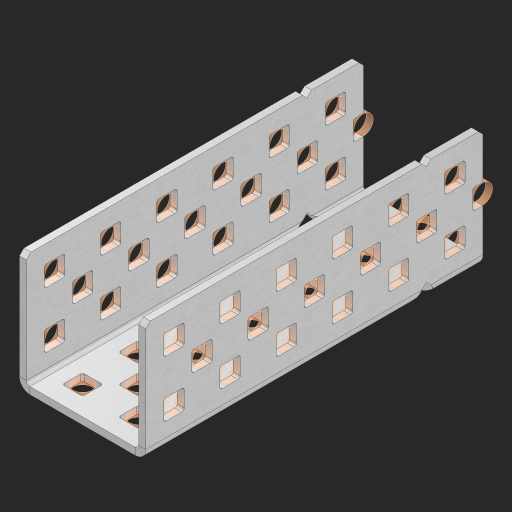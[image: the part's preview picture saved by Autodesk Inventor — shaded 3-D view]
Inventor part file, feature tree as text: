
AUTODESK INVENTOR PART (.ipt)
format: ipt  version: 2023 (Build 270158000, 158)  size: 1,067,520 bytes
history: native  units: in
note: dims shown in document units (in); Inventor stores cm internally (conversion verified against a paired STEP export)
features: other x78, extrude x70, sheet_metal_op x8, sketch x7, mirror x3, pattern_linear x2, chamfer x1
ambient origin geometry x8: Origin, YZ Plane, XZ Plane, XY Plane, X Axis, Y Axis, Z Axis, Center Point
bodies: Solid1 (feature_tree), Body (feature_tree)
feature tree (169):
  sheet_metal_op  "Flanges"
  sheet_metal_op  "Body Pattern"
  pattern_linear  "Center Pattern"  Spacing1=1.0in  [1 undecoded]
  other  "Arc Length"
  mirror  "Notch Mirror"
  pattern_linear  "Notch Pattern"  Spacing1=0.25in  [1 undecoded]
  other  "Diagonal Plane"
  mirror  "Flange 1"
  mirror  "Flange 2"
  chamfer  "End Chamfer"
  sketch  "Sketch1"  dims[d0=1.0in]
  other  "Plate1"
  sketch  "Sketch2"  dims[d1=3.0in]
  other  "Plate2"
  sheet_metal_op  "Bend1"
  sheet_metal_op  "Corner1"
  sketch  "Sketch8"  dims[d2=0.0625in]
  sketch  "Sketch9"  dims[d3=0.0625in]
  other  "Srf91"
  sheet_metal_op  "Body Pattern Sketch"
  other  "Srf92"
  sketch  "Sketch13"  dims[d4=0.0312in]
  sketch  "Sketch15"  dims[d5=0.125in]
  sketch  "Sketch16"  dims[d6=0.0625in d7=1.0in d8=90.0deg d9=0.0312in d10=0.25in d11=0.0625in d12=0.0625in d49=0.182in d50=0.02in d52=0.25in d53=0.0625in d54=0.0in d55=0.172in d56=1.0in d57=0.0in d60=2.3622in d62=0.5in d63=0.7874in d65=0.5in d85=0.1473in d86=0.1782in d88=0.04in d89=0.0625in d90=0.0in d91=0.04in d92=0.0491in d95=2.5in d96=0.04in d97=0.25in d98=45.0deg d99=0.25in d102=2.497in d106=0.182in d107=0.02in d108=0.5in d110=0.0625in d111=0.0in d112=0.172in d113=0.5in d114=0.0in d117=0.5in d118=0.5in d131=0.25in d132=0.25in]
  other  "Srf786"
  other  "Srf889"
  other  "Srf890"
  other  "Srf891"
  other  "Srf892"
  other  "Srf893"
  other  "Srf1315"
  other  "Srf1316"
  other  "Srf1317"
  other  "Srf1325"
  other  "Srf1326"
  other  "Srf1327"
  other  "Srf1328"
  other  "Srf1329"
  other  "Srf1374"
  other  "Srf1375"
  other  "Srf1376"
  other  "Srf1384"
  other  "Srf1385"
  other  "Srf1386"
  other  "Srf1387"
  other  "Srf1388"
  other  "Srf1433"
  other  "Srf1434"
  other  "Srf1473"
  other  "Srf1474"
  other  "Srf1475"
  other  "Srf1476"
  other  "Srf1477"
  other  "Srf1478"
  other  "Srf1500"
  other  "Srf1501"
  other  "Srf1502"
  other  "Srf1503"
  other  "Srf1504"
  other  "Srf1505"
  other  "Srf1506"
  other  "Srf1507"
  other  "Srf1508"
  other  "Srf1509"
  other  "Srf1538"
  other  "Srf1539"
  other  "Srf1540"
  other  "Srf1541"
  other  "Srf1542"
  other  "Srf1543"
  other  "Srf1544"
  other  "Srf1545"
  other  "Srf1546"
  other  "Srf1547"
  other  "Srf1576"
  other  "Srf1577"
  other  "Srf1578"
  other  "Srf1579"
  other  "Srf1580"
  other  "Srf1581"
  other  "Srf1582"
  other  "Srf1583"
  other  "Srf1584"
  other  "Srf1585"
  other  "Srf1614"
  other  "Srf1615"
  other  "Srf1616"
  other  "Srf1617"
  other  "Srf1618"
  other  "Srf1619"
  other  "Srf1620"
  other  "Srf1621"
  other  "Srf1622"
  other  "Srf1623"
  sheet_metal_op  "Body Stamp"
  sheet_metal_op  "Body Circle"
  other  "Center Stamp"
  other  "Center Circle"
  sheet_metal_op  "Notch"
  extrude  "ExtrusionSrf92"  Depth=0.0625in
  extrude  "ExtrusionSrf889"  Depth=0.0625in
  extrude  "ExtrusionSrf890"  Depth=0.182in
  extrude  "ExtrusionSrf891"  Depth=0.02in
  extrude  "ExtrusionSrf892"  Depth=0.25in
  extrude  "ExtrusionSrf893"  Depth=0.0625in
  extrude  "ExtrusionSrf1315"  TaperAngle=0.0deg  [1 undecoded]
  extrude  "ExtrusionSrf1316"  Depth=0.25in
  extrude  "ExtrusionSrf1355"  Depth=1.0in TaperAngle=0.0deg
  extrude  "ExtrusionSrf1356"  Depth=0.25in
  extrude  "ExtrusionSrf1357"  Depth=0.5in
  extrude  "ExtrusionSrf1358"  Depth=0.25in
  extrude  "ExtrusionSrf1359"  Depth=0.25in
  extrude  "ExtrusionSrf1360"  Depth=0.25in
  extrude  "ExtrusionSrf1374"  Depth=0.0625in
  extrude  "ExtrusionSrf1375"  TaperAngle=0.0deg  [1 undecoded]
  extrude  "ExtrusionSrf1414"  Depth=0.25in
  extrude  "ExtrusionSrf1415"  Depth=0.25in
  extrude  "ExtrusionSrf1416"  Depth=2.5in
  extrude  "ExtrusionSrf1417"  Depth=0.25in TaperAngle=45.0deg
  extrude  "ExtrusionSrf1418"  Depth=0.25in
  extrude  "ExtrusionSrf1419"  Depth=0.25in
  extrude  "ExtrusionSrf1433"  Depth=0.182in
  extrude  "ExtrusionSrf1434"  Depth=0.02in
  extrude  "ExtrusionSrf1473"  Depth=0.5in
  extrude  "ExtrusionSrf1474"  Depth=0.0625in
  extrude  "ExtrusionSrf1475"  TaperAngle=0.0deg  [1 undecoded]
  extrude  "ExtrusionSrf1476"  Depth=0.25in
  extrude  "ExtrusionSrf1477"  Depth=0.5in TaperAngle=0.0deg
  extrude  "ExtrusionSrf1478"  Depth=0.5in
  extrude  "ExtrusionSrf1500"  Depth=0.5in
  extrude  "ExtrusionSrf1501"  Depth=0.25in
  extrude  "ExtrusionSrf1502"  Depth=0.25in
  extrude  "ExtrusionSrf1503"  [1 undecoded]
  extrude  "ExtrusionSrf1504"  [1 undecoded]
  extrude  "ExtrusionSrf1505"  [1 undecoded]
  extrude  "ExtrusionSrf1506"  [1 undecoded]
  extrude  "ExtrusionSrf1507"  [1 undecoded]
  extrude  "ExtrusionSrf1508"  [1 undecoded]
  extrude  "ExtrusionSrf1509"  [1 undecoded]
  extrude  "ExtrusionSrf1538"  [1 undecoded]
  extrude  "ExtrusionSrf1539"  [1 undecoded]
  extrude  "ExtrusionSrf1540"  [1 undecoded]
  extrude  "ExtrusionSrf1541"  [1 undecoded]
  extrude  "ExtrusionSrf1542"  [1 undecoded]
  extrude  "ExtrusionSrf1543"  [1 undecoded]
  extrude  "ExtrusionSrf1544"  [1 undecoded]
  extrude  "ExtrusionSrf1545"  [1 undecoded]
  extrude  "ExtrusionSrf1546"  [1 undecoded]
  extrude  "ExtrusionSrf1547"  [1 undecoded]
  extrude  "ExtrusionSrf1576"  [1 undecoded]
  extrude  "ExtrusionSrf1577"  [1 undecoded]
  extrude  "ExtrusionSrf1578"  [1 undecoded]
  extrude  "ExtrusionSrf1579"  [1 undecoded]
  extrude  "ExtrusionSrf1580"  [1 undecoded]
  extrude  "ExtrusionSrf1581"  [1 undecoded]
  extrude  "ExtrusionSrf1582"  [1 undecoded]
  extrude  "ExtrusionSrf1583"  [1 undecoded]
  extrude  "ExtrusionSrf1584"  [1 undecoded]
  extrude  "ExtrusionSrf1585"  [1 undecoded]
  extrude  "ExtrusionSrf1614"  [1 undecoded]
  extrude  "ExtrusionSrf1615"  [1 undecoded]
  extrude  "ExtrusionSrf1616"  [1 undecoded]
  extrude  "ExtrusionSrf1617"  [1 undecoded]
  extrude  "ExtrusionSrf1618"  [1 undecoded]
  extrude  "ExtrusionSrf1619"  [1 undecoded]
  extrude  "ExtrusionSrf1620"  [1 undecoded]
  extrude  "ExtrusionSrf1621"  [1 undecoded]
  extrude  "ExtrusionSrf1622"  [1 undecoded]
  extrude  "ExtrusionSrf1623"  [1 undecoded]
note: 42 required parameter values undecoded (feature->parameter linkage not recoverable at this tier; creation-order binding heuristic only, values carry confidence <= 0.55)
